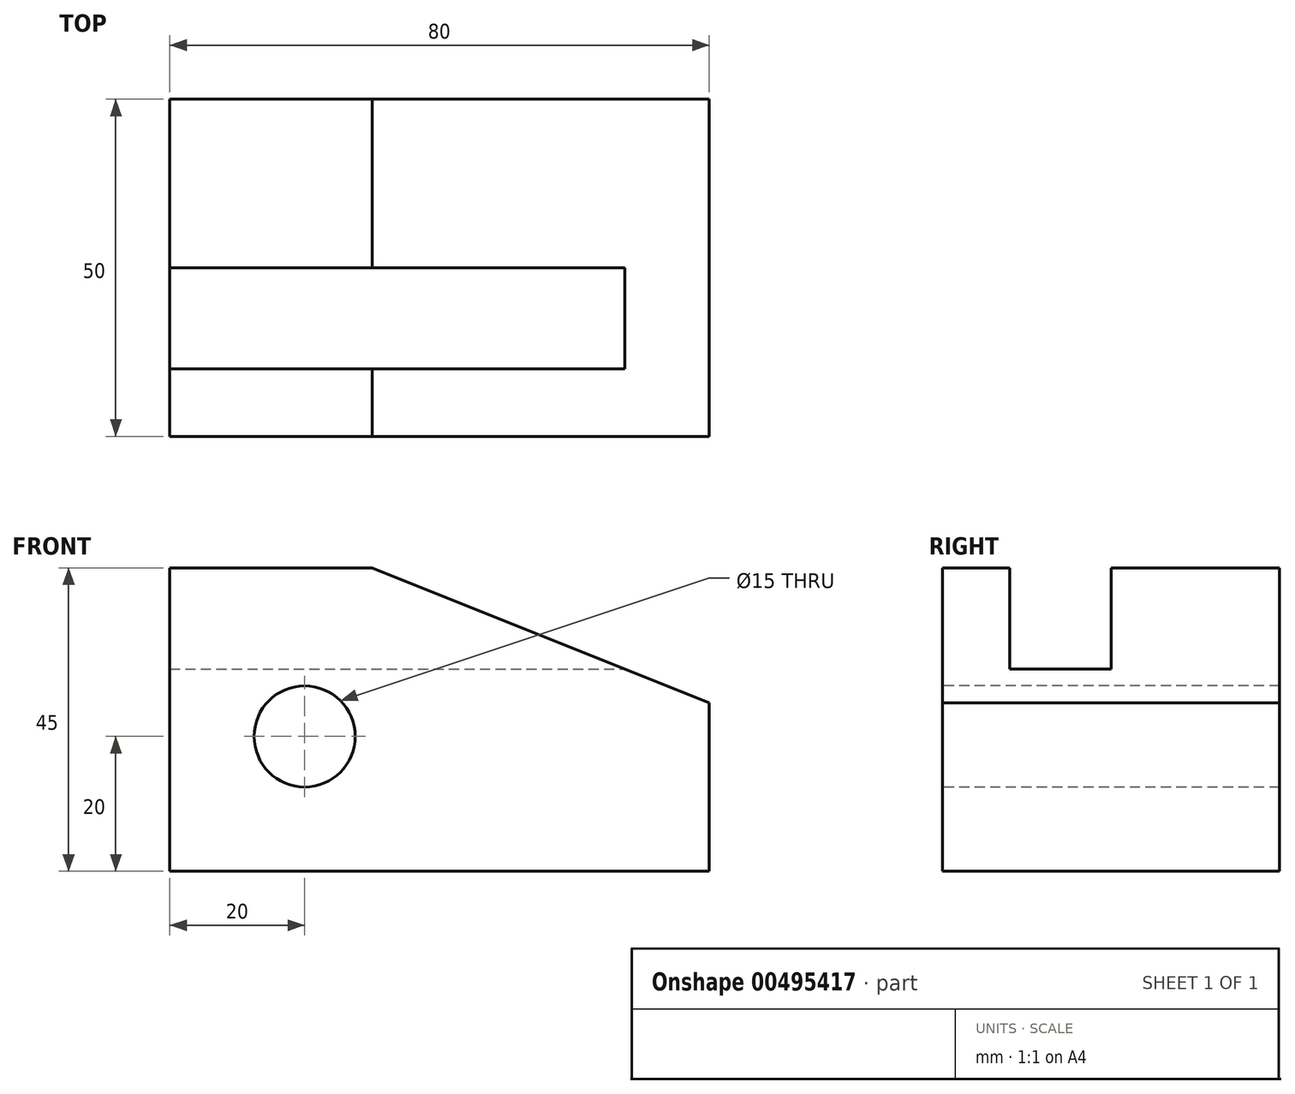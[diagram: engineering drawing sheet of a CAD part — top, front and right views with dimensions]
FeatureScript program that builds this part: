
annotation { "Feature Type Name" : "Feature", "Feature Type Description" : "" }
export const myFeature = defineFeature(function(context is Context, id is Id, definition is map)
    precondition{}
    {
        {
            var Q0;
            Q0=qCreatedBy(makeId("Front.planeOp"),FACE);
            var sketch = newSketch(context, id + "F0", { "sketchPlane" : qUnion([Q0])});
            skLineSegment(sketch, "E0", {"start": v(0, 0) * mm, "end": v(0, 45) * mm});
            skLineSegment(sketch, "E1", {"start": v(0, 45) * mm, "end": v(30, 45) * mm});
            skLineSegment(sketch, "E2", {"start": v(30, 45) * mm, "end": v(80, 25) * mm});
            skLineSegment(sketch, "E3", {"start": v(80, 25) * mm, "end": v(80, 0) * mm});
            skLineSegment(sketch, "E4", {"start": v(80, 0) * mm, "end": v(0, 0) * mm});
            skSolve(sketch);
        }
        {
            var Q0;
            Q0=qSketchRegion(id+"F0",true);
            extrude(context, id + "F1", {"entities" : qUnion([Q0]), "depth" : 50 * mm});
        }
        {
            var Q0;
            Q0=makeQuery(id+"F1.opExtrude","CAP_FACE",FACE,{"disambiguationData":[OSD([sQuery(id+"F0.wireOp",EDGE,"E0"),sQuery(id+"F0.wireOp",EDGE,"E1"),sQuery(id+"F0.wireOp",EDGE,"E2"),sQuery(id+"F0.wireOp",EDGE,"E3"),sQuery(id+"F0.wireOp",EDGE,"E4")])],"isStart":false});
            var sketch = newSketch(context, id + "F2", { "sketchPlane" : qUnion([Q0])});
            skCircle(sketch, "E5", {"center": v(20, 20) * mm, "radius": 7.5 * mm});
            skSolve(sketch);
        }
        {
            var Q0;
            Q0=qSketchRegion(id+"F2",true);
            extrude(context, id + "F3", {"entities" : qUnion([Q0]), "operationType" : NewBodyOperationType.REMOVE, "endBound" : BoundingType.THROUGH_ALL, "oppositeDirection" : true, "depth" : 25 * mm});
        }
        {
            var Q0;
            Q0=makeQuery(id+"F1.opExtrude","SWEPT_FACE",FACE,{"disambiguationData":[OSD([sQuery(id+"F0.wireOp",EDGE,"E4")])]});
            cPlane(context, id + "F4", {"entities" : qUnion([Q0]), "cplaneType" : CPlaneType.OFFSET, "offset" : 30 * mm, "oppositeDirection" : true, "width" : 150 * mm, "height" : 150 * mm});
        }
        {
            var Q0;
            Q0=makeQuery(id+"F1.opExtrude","SWEPT_FACE",FACE,{"disambiguationData":[OSD([sQuery(id+"F0.wireOp",EDGE,"E1")])]});
            var sketch = newSketch(context, id + "F5", { "sketchPlane" : qUnion([Q0])});
            skLineSegment(sketch, "E6.bottom", {"start": v(0, -40) * mm, "end": v(80, -40) * mm});
            skLineSegment(sketch, "E6.top", {"start": v(0, -25) * mm, "end": v(80, -25) * mm});
            skLineSegment(sketch, "E6.left", {"start": v(0, -40) * mm, "end": v(0, -25) * mm});
            skLineSegment(sketch, "E6.right", {"start": v(80, -40) * mm, "end": v(80, -25) * mm});
            skSolve(sketch);
        }
        {
            var Q0;
            Q0=qSketchRegion(id+"F5",true);
            var Q1;
            Q1=qCreatedBy(id+"F4.planeOp",FACE);
            extrude(context, id + "F6", {"entities" : qUnion([Q0]), "operationType" : NewBodyOperationType.REMOVE, "endBound" : BoundingType.UP_TO_SURFACE, "oppositeDirection" : true, "endBoundEntityFace" : qUnion([Q1]), "depth" : 25 * mm});
        }
    });
